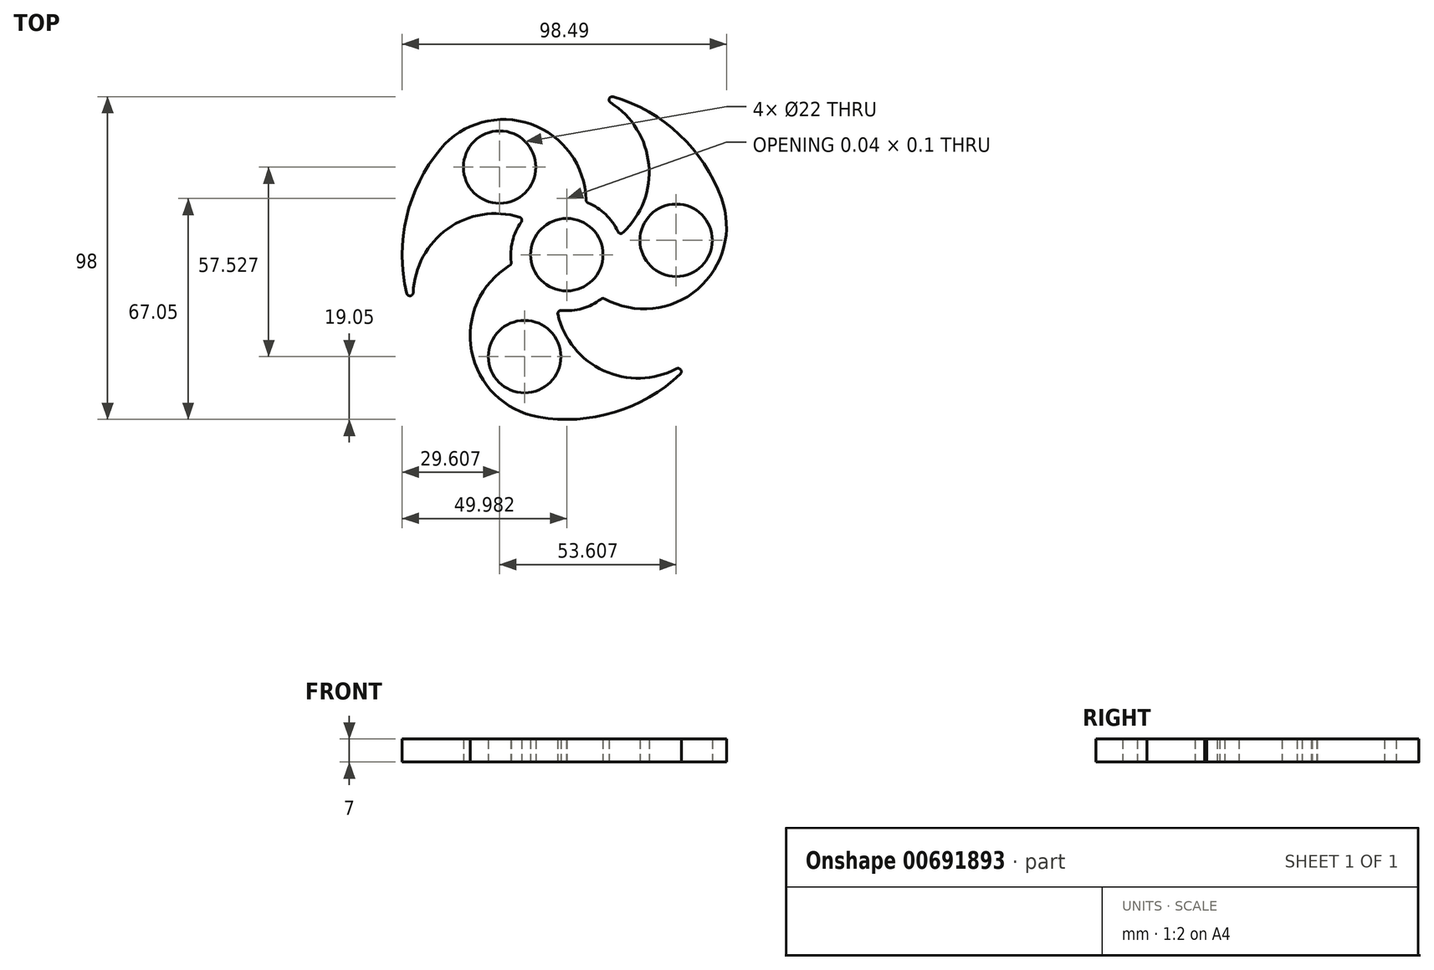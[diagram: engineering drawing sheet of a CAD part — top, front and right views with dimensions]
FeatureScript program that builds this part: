
annotation { "Feature Type Name" : "Feature", "Feature Type Description" : "" }
export const myFeature = defineFeature(function(context is Context, id is Id, definition is map)
    precondition{}
    {
        {
            var Q0;
            Q0=qCreatedBy(makeId("Top.planeOp"),FACE);
            var sketch = newSketch(context, id + "F0", { "sketchPlane" : qUnion([Q0])});
            skArc(sketch, "E0", {"start": v(46.98, 17.1) * mm, "mid": v(34.24, 36.44) * mm, "end": v(14.14, 47.96) * mm});
            skCircle(sketch, "E1", {"center": v(0, 0) * mm, "radius": 11 * mm});
            skArc(sketch, "E2", {"start": v(-13.84, 9.88) * mm, "mid": v(-16.5, 4.1) * mm, "end": v(-16.85, -2.27) * mm});
            skArc(sketch, "E3", {"start": v(17.06, 6.73) * mm, "mid": v(24.89, 27.36) * mm, "end": v(13.32, 46.15) * mm});
            skLineSegment(sketch, "E4", {"start": v(15.97, 5.81) * mm, "end": v(16.07, 5.85) * mm});
            skArc(sketch, "E5", {"start": v(0, 17.1) * mm, "mid": v(-0.02, 17.05) * mm, "end": v(-0.04, 17) * mm});
            skArc(sketch, "E6.trimOffspring", {"start": v(-8.68, -49.24) * mm, "mid": v(14.44, -47.87) * mm, "end": v(34.46, -36.22) * mm});
            skArc(sketch, "E7.trimOffspring", {"start": v(-38.3, 32.14) * mm, "mid": v(-48.68, 11.43) * mm, "end": v(-48.6, -11.73) * mm});
            skArc(sketch, "E8.trimOffspring", {"start": v(-14.36, 11.41) * mm, "mid": v(-36.14, 7.87) * mm, "end": v(-46.63, -11.54) * mm});
            skLineSegment(sketch, "E9.trimOffspring", {"start": v(0, 17) * mm, "end": v(0, 17.1) * mm});
            skArc(sketch, "E10.trimOffspring", {"start": v(-17.32, -3.25) * mm, "mid": v(-28.91, -29.24) * mm, "end": v(-8.68, -49.24) * mm});
            skArc(sketch, "E11.trimOffspring", {"start": v(-2.7, -18.14) * mm, "mid": v(11.25, -35.23) * mm, "end": v(33.3, -34.62) * mm});
            skArc(sketch, "E12.trimOffspring", {"start": v(11.48, -13.37) * mm, "mid": v(39.77, -10.42) * mm, "end": v(46.98, 17.1) * mm});
            skArc(sketch, "E13.trimOffspring", {"start": v(5.84, 16.63) * mm, "mid": v(-10.86, 39.66) * mm, "end": v(-38.3, 32.14) * mm});
            skArc(sketch, "E14.trimOffspring", {"start": v(0, 17) * mm, "mid": v(-0.02, 17) * mm, "end": v(-0.04, 17) * mm});
            skArc(sketch, "E15.trimOffspring", {"start": v(15.47, 7.05) * mm, "mid": v(11.8, 12.24) * mm, "end": v(6.46, 15.72) * mm});
            skArc(sketch, "E16.trimOffspring", {"start": v(-1.63, -16.92) * mm, "mid": v(4.7, -16.34) * mm, "end": v(10.39, -13.46) * mm});
            skLineSegment(sketch, "E17", {"start": v(0, 0) * mm, "end": v(-30.44, 39.67) * mm});
            skCircle(sketch, "E18", {"center": v(-20.4, 26.58) * mm, "radius": 11 * mm});
            skCircle(sketch, "E19.1.0", {"center": v(-12.82, -30.95) * mm, "radius": 11 * mm});
            skCircle(sketch, "E19.2.0", {"center": v(33.21, 4.37) * mm, "radius": 11 * mm});
            skPoint(sketch, "E20.visualSharp", {"position": v(0, 50) * mm});
            skArc(sketch, "E20.filletArc", {"start": v(14.14, 47.96) * mm, "mid": v(12.95, 47.41) * mm, "end": v(13.32, 46.15) * mm});
            skPoint(sketch, "E21.visualSharp", {"position": v(43.3, -25) * mm});
            skArc(sketch, "E21.filletArc", {"start": v(34.46, -36.22) * mm, "mid": v(34.59, -34.92) * mm, "end": v(33.3, -34.62) * mm});
            skPoint(sketch, "E22.visualSharp", {"position": v(-43.3, -25) * mm});
            skArc(sketch, "E22.filletArc", {"start": v(-48.6, -11.73) * mm, "mid": v(-47.53, -12.5) * mm, "end": v(-46.63, -11.54) * mm});
            skPoint(sketch, "E23.visualSharp", {"position": v(-16.75, -2.92) * mm});
            skArc(sketch, "E23.filletArc", {"start": v(-17.32, -3.25) * mm, "mid": v(-16.94, -2.83) * mm, "end": v(-16.85, -2.27) * mm});
            skPoint(sketch, "E24.visualSharp", {"position": v(-13, 10.96) * mm});
            skArc(sketch, "E24.filletArc", {"start": v(-13.84, 9.88) * mm, "mid": v(-13.7, 10.78) * mm, "end": v(-14.36, 11.41) * mm});
            skPoint(sketch, "E25.visualSharp", {"position": v(5.85, 15.96) * mm});
            skArc(sketch, "E25.filletArc", {"start": v(5.84, 16.63) * mm, "mid": v(6.02, 16.08) * mm, "end": v(6.46, 15.72) * mm});
            skPoint(sketch, "E26.visualSharp", {"position": v(15.99, 5.78) * mm});
            skArc(sketch, "E26.filletArc", {"start": v(15.47, 7.05) * mm, "mid": v(16.19, 6.48) * mm, "end": v(17.06, 6.73) * mm});
            skPoint(sketch, "E27.visualSharp", {"position": v(10.9, -13.05) * mm});
            skArc(sketch, "E27.filletArc", {"start": v(11.48, -13.37) * mm, "mid": v(10.92, -13.25) * mm, "end": v(10.39, -13.46) * mm});
            skPoint(sketch, "E28.visualSharp", {"position": v(-2.99, -16.74) * mm});
            skArc(sketch, "E28.filletArc", {"start": v(-1.63, -16.92) * mm, "mid": v(-2.48, -17.26) * mm, "end": v(-2.7, -18.14) * mm});
            skSolve(sketch);
        }
        {
            var Q0;
            Q0 = qSketchRegion(id + "F0", true);
            extrude(context, id + "F1", {"entities" : qUnion([Q0]), "depth" : 7 * mm, "offsetDistance" : 25 * mm});
        }
    });
